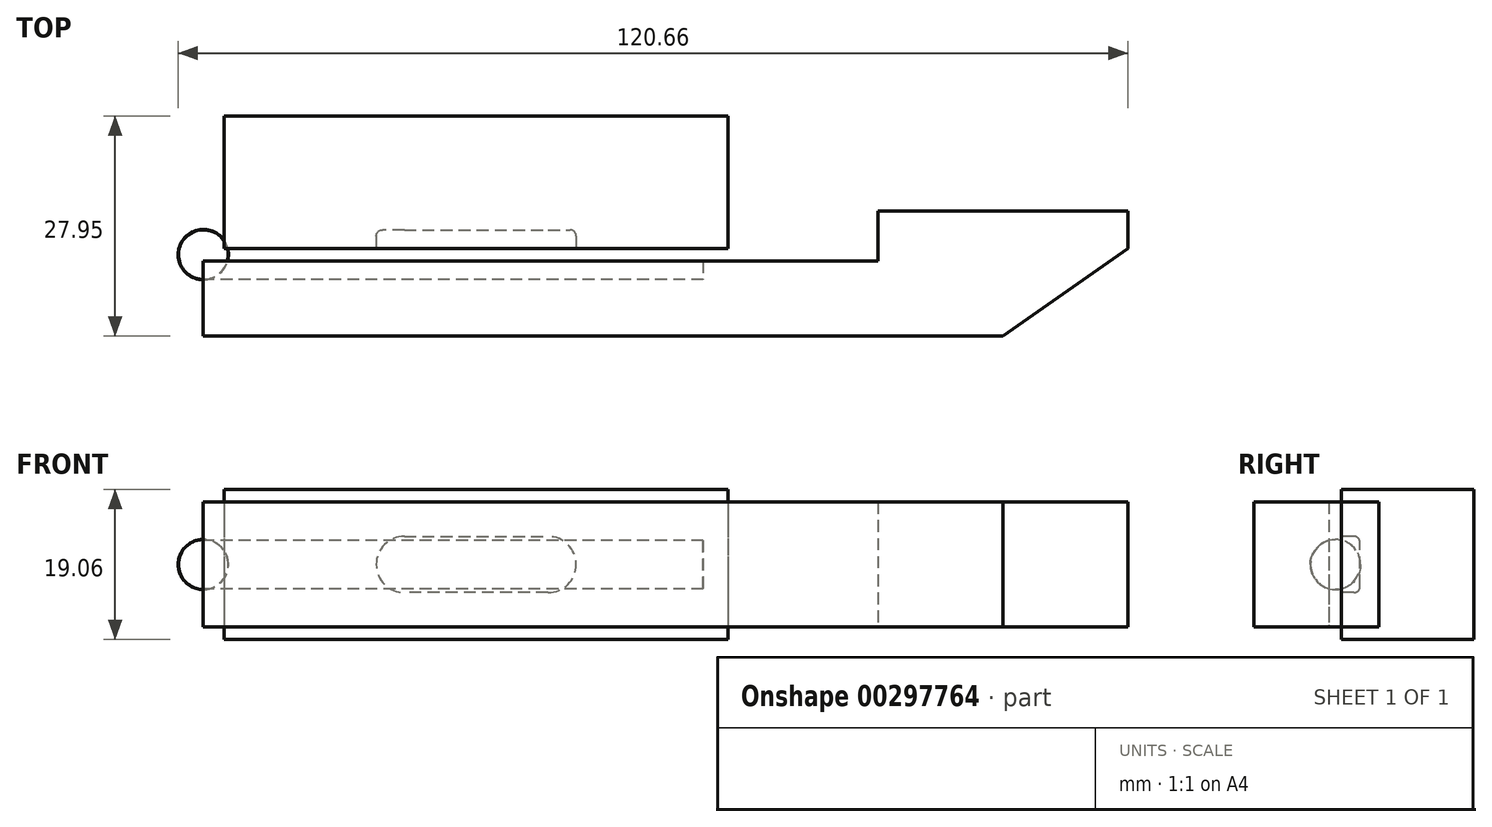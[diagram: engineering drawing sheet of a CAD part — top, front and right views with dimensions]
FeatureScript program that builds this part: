
annotation { "Feature Type Name" : "Feature", "Feature Type Description" : "" }
export const myFeature = defineFeature(function(context is Context, id is Id, definition is map)
    precondition{}
    {
        {
            var Q0;
            Q0=qCreatedBy(makeId("Top.planeOp"),FACE);
            var sketch = newSketch(context, id + "F0", { "sketchPlane" : qUnion([Q0])});
            skLineSegment(sketch, "E0.bottom", {"start": v(-32, 8.42) * mm, "end": v(32, 8.42) * mm});
            skLineSegment(sketch, "E0.top", {"start": v(-32, -8.42) * mm, "end": v(32, -8.42) * mm});
            skLineSegment(sketch, "E0.left", {"start": v(-32, 8.42) * mm, "end": v(-32, -8.42) * mm});
            skLineSegment(sketch, "E0.right", {"start": v(32, 8.42) * mm, "end": v(32, -8.42) * mm});
            skLineSegment(sketch, "E1", {"start": v(-34.67, -10) * mm, "end": v(-34.67, -19.53) * mm});
            skLineSegment(sketch, "E2", {"start": v(-34.67, -19.53) * mm, "end": v(66.93, -19.53) * mm});
            skLineSegment(sketch, "E3", {"start": v(66.93, -19.53) * mm, "end": v(82.8, -8.42) * mm});
            skLineSegment(sketch, "E4", {"start": v(-34.67, -10) * mm, "end": v(51.05, -10) * mm});
            skLineSegment(sketch, "E5", {"start": v(51.05, -3.65) * mm, "end": v(51.05, -10) * mm});
            skLineSegment(sketch, "E6", {"start": v(51.05, -3.65) * mm, "end": v(82.8, -3.65) * mm});
            skLineSegment(sketch, "E7", {"start": v(82.8, -3.65) * mm, "end": v(82.8, -8.42) * mm});
            skSolve(sketch);
        }
        {
            var Q0;
            Q0=makeQuery(id+"F0.imprint","IMPRINT",FACE,{"disambiguationData":[TD([[makeQuery(id+"F0.imprint","IMPRINT",EDGE,{"derivedFrom":sQuery(id+"F0.wireOp",EDGE,"E0.bottom")}),-1.0]])]});
            extrude(context, id + "F1", {"entities" : qUnion([Q0]), "endBound" : BoundingType.SYMMETRIC, "depth" : 19.05 * mm});
        }
        {
            var Q0;
            Q0=makeQuery(id+"F0.imprint","IMPRINT",FACE,{"disambiguationData":[TD([[makeQuery(id+"F0.imprint","IMPRINT",EDGE,{"derivedFrom":sQuery(id+"F0.wireOp",EDGE,"E1")}),1.0]])]});
            extrude(context, id + "F2", {"entities" : qUnion([Q0]), "endBound" : BoundingType.SYMMETRIC, "depth" : 15.88 * mm});
        }
        {
            var Q0;
            Q0=makeQuery(id+"F2.opExtrude","SWEPT_FACE",FACE,{"disambiguationData":[OSD([sQuery(id+"F0.wireOp",EDGE,"E1")])]});
            var sketch = newSketch(context, id + "F3", { "sketchPlane" : qUnion([Q0])});
            skCircle(sketch, "E8", {"center": v(9.2, 0) * mm, "radius": 3.18 * mm});
            skPoint(sketch, "E8.centerSnap0", {"position": v(10, 0) * mm});
            skLineSegment(sketch, "E9", {"start": v(9.19, 3.17) * mm, "end": v(9.19, -3.17) * mm});
            skSolve(sketch);
        }
        {
            var Q0;
            {var subQ0=sQuery(id+"F3.wireOp",EDGE,"E8");var subQ1=makeQuery(id+"F2.opExtrude","SWEPT_EDGE",EDGE,{"disambiguationData":[OSD([sQuery(id+"F0.wireOp",EDGE,"E1"),sQuery(id+"F0.wireOp",EDGE,"E4")])]});var subQ2=makeQuery(id+"F3.imprint","INTERSECT",VERTEX,{"disambiguationData":[OD(0.0)],"derivedFrom":[subQ1,subQ0]});Q0=makeQuery(id+"F3.imprint","IMPRINT",FACE,{"disambiguationData":[TD([[makeQuery(id+"F3.imprint","IMPRINT",EDGE,{"disambiguationData":[TD([[subQ2,-1.0]])],"derivedFrom":subQ0}),1.0]])]});}
            extrude(context, id + "F4", {"entities" : qUnion([Q0]), "operationType" : NewBodyOperationType.REMOVE, "oppositeDirection" : true, "depth" : 63.5 * mm});
        }
        {
            var Q0;
            Q0=makeQuery(id+"F1.opExtrude","SWEPT_FACE",FACE,{"disambiguationData":[OSD([sQuery(id+"F0.wireOp",EDGE,"E0.top")])]});
            var sketch = newSketch(context, id + "F5", { "sketchPlane" : qUnion([Q0])});
            skArc(sketch, "E10", {"start": v(-9.13, 3.57) * mm, "mid": v(-12.7, 0) * mm, "end": v(-9.13, -3.57) * mm});
            skArc(sketch, "E11", {"start": v(9.13, -3.57) * mm, "mid": v(12.7, 0) * mm, "end": v(9.13, 3.57) * mm});
            skLineSegment(sketch, "E12", {"start": v(-9.13, 3.57) * mm, "end": v(9.13, 3.57) * mm});
            skLineSegment(sketch, "E13", {"start": v(9.13, -3.57) * mm, "end": v(-9.13, -3.57) * mm});
            skSolve(sketch);
        }
        {
            var Q0;
            Q0=makeQuery(id+"F5.imprint","IMPRINT",FACE,{"disambiguationData":[TD([[makeQuery(id+"F5.imprint","IMPRINT",EDGE,{"derivedFrom":sQuery(id+"F5.wireOp",EDGE,"E10")}),1.0]])]});
            extrude(context, id + "F6", {"entities" : qUnion([Q0]), "operationType" : NewBodyOperationType.REMOVE, "oppositeDirection" : true, "depth" : 2.36 * mm});
        }
        {
            var Q0;
            Q0=makeQuery(id+"F6.boolean.opBoolean","COPY",FACE,{"derivedFrom":makeQuery(id+"F6.opExtrude","CAP_FACE",FACE,{"disambiguationData":[OSD([sQuery(id+"F5.wireOp",EDGE,"E10"),sQuery(id+"F5.wireOp",EDGE,"E11"),sQuery(id+"F5.wireOp",EDGE,"E12"),sQuery(id+"F5.wireOp",EDGE,"E13")])],"isStart":false})});
            var Q1;
            Q1=makeQuery(id+"F6.boolean.opBoolean","COPY",EDGE,{"derivedFrom":makeQuery(id+"F6.opExtrude","CAP_EDGE",EDGE,{"disambiguationData":[OSD([sQuery(id+"F5.wireOp",EDGE,"E10")])],"isStart":true})});
            fillet(context, id + "F7", {"entities" : qUnion([Q0, Q1]), "radius" : 0.8 * mm, "tangentPropagation" : true, "allowEdgeOverflow" : false});
        }
        {
            var Q0;
            {var subQ0=sQuery(id+"F3.wireOp",EDGE,"E9");Q0=makeQuery(id+"F3.imprint","IMPRINT",FACE,{"disambiguationData":[TD([[makeQuery(id+"F3.imprint","IMPRINT",EDGE,{"derivedFrom":subQ0}),-1.0]])]});}
            var Q1;
            Q1=sQuery(id+"F3.wireOp",EDGE,"E9");
            revolve(context, id + "F8", {"entities" : qUnion([Q0]), "axis" : qUnion([Q1]), "revolveType" : RevolveType.FULL});
        }
    });
